FCSTD DOCUMENT  (FreeCAD 0.20R29603 (Git))
Label: Heat Exchanger inlet dispersion grid rounded edges - 100mm
License: All rights reserved
LicenseURL: http://en.wikipedia.org/wiki/All_rights_reserved
objects: Sketcher::SketchObject×6, PartDesign::Body×1
note: 7 computed .brp shape members not serialized (recipe doc carries the construction recipe); baked Part::Feature solids carry a one-line shape summary decoded from their .brp

FEATURE [Sketcher::SketchObject] Sketch
  FullyConstrained = false
  MapMode = 5
  Support = -> [XY_Plane]
  sketch-geometry (86):
    g0: ArcOfCircle CenterX=0 CenterY=0 CenterZ=0 NormalX=0 NormalY=0 NormalZ=1 AngleXU=0 Radius=114.286 StartAngle=0 EndAngle=1.5708
    g1: LineSegment StartX=32.431 StartY=109.588 StartZ=0 EndX=49.5867 EndY=102.968 EndZ=0
    g2: LineSegment StartX=56.0034 StartY=99.6235 StartZ=0 EndX=71.256 EndY=89.3522 EndZ=0
    g3: LineSegment StartX=76.7676 StartY=84.6638 StartZ=0 EndX=89.3522 EndY=71.256 EndZ=0
    g4: LineSegment StartX=93.6823 StartY=65.4587 StartZ=0 EndX=102.968 EndY=49.5867 EndZ=0
    g5: LineSegment StartX=105.903 StartY=42.9634 StartZ=0 EndX=111.422 EndY=25.4227 EndZ=0
    g6: LineSegment StartX=14.2857 StartY=2.955e-12 StartZ=0 EndX=0 EndY=2.955e-12 EndZ=0
    g7: LineSegment StartX=28.5714 StartY=2.955e-12 StartZ=0 EndX=14.2857 EndY=2.955e-12 EndZ=0
    g8: LineSegment StartX=57.1429 StartY=2.955e-12 StartZ=0 EndX=42.8571 EndY=2.955e-12 EndZ=0
    g9: LineSegment StartX=42.8571 StartY=2.955e-12 StartZ=0 EndX=28.5714 EndY=2.955e-12 EndZ=0
    g10: LineSegment StartX=71.4286 StartY=2.955e-12 StartZ=0 EndX=57.1429 EndY=2.955e-12 EndZ=0
    g11: LineSegment StartX=85.7143 StartY=2.955e-12 StartZ=0 EndX=71.4286 EndY=2.955e-12 EndZ=0
    g12: LineSegment StartX=85.7143 StartY=2.955e-12 StartZ=0 EndX=100 EndY=2.955e-12 EndZ=0
    g13: LineSegment StartX=100 StartY=2.955e-12 StartZ=0 EndX=114.286 EndY=2.955e-12 EndZ=0
    g14: LineSegment StartX=14.2857 StartY=2.955e-12 StartZ=0 EndX=14.2857 EndY=10 EndZ=0
    g15: LineSegment StartX=32.431 StartY=109.588 StartZ=0 EndX=28.9234 EndY=9.9938 EndZ=0
    g16: LineSegment StartX=28.9234 StartY=9.9938 StartZ=0 EndX=28.5714 EndY=2.9559e-12 EndZ=0
    g17: LineSegment StartX=56.0034 StartY=99.6235 StartZ=0 EndX=44.1654 EndY=9.91405 EndZ=0
    g18: LineSegment StartX=44.1654 StartY=9.91405 StartZ=0 EndX=42.8571 EndY=2.9559e-12 EndZ=0
    g19: LineSegment StartX=76.7676 StartY=84.6638 StartZ=0 EndX=59.4009 EndY=9.74172 EndZ=0
    g20: LineSegment StartX=59.4009 StartY=9.74172 StartZ=0 EndX=57.1429 EndY=2.9559e-12 EndZ=0
    g21: LineSegment StartX=93.6823 StartY=65.4587 StartZ=0 EndX=74.6473 EndY=9.46782 EndZ=0
    g22: LineSegment StartX=74.6473 StartY=9.46782 StartZ=0 EndX=71.4286 EndY=2.9559e-12 EndZ=0
    g23: LineSegment StartX=105.903 StartY=42.9634 StartZ=0 EndX=89.9671 EndY=9.05059 EndZ=0
    g24: LineSegment StartX=89.9671 StartY=9.05059 StartZ=0 EndX=85.7143 EndY=2.9559e-12 EndZ=0
    g25: GeomPoint X=65.1429 Y=157.269 Z=0
    g26: Circle CenterX=49.5867 CenterY=102.968 CenterZ=0 NormalX=0 NormalY=0 NormalZ=1 AngleXU=0 Radius=1
    g27: Circle CenterX=30.8258 CenterY=64.0104 CenterZ=0 NormalX=0 NormalY=0 NormalZ=1 AngleXU=0 Radius=1
    g28: Circle CenterX=28.9234 CenterY=9.9938 CenterZ=0 NormalX=0 NormalY=0 NormalZ=1 AngleXU=0 Radius=1
    g29: BSplineCurve PolesCount=3 KnotsCount=2 Degree=2 IsPeriodic=0
    g30: GeomPoint X=49.5867 Y=102.968 Z=0
    g31: GeomPoint X=28.9234 Y=9.9938 Z=0
    g32: LineSegment StartX=49.5867 StartY=102.968 StartZ=0 EndX=30.8258 EndY=64.0104 EndZ=0
    g33: Circle CenterX=71.256 CenterY=89.3522 CenterZ=0 NormalX=0 NormalY=0 NormalZ=1 AngleXU=0 Radius=1
    g34: Circle CenterX=51.3549 CenterY=64.3971 CenterZ=0 NormalX=0 NormalY=0 NormalZ=1 AngleXU=0 Radius=1
    g35: Circle CenterX=44.1654 CenterY=9.91405 CenterZ=0 NormalX=0 NormalY=0 NormalZ=1 AngleXU=0 Radius=1
    g36: BSplineCurve PolesCount=3 KnotsCount=2 Degree=2 IsPeriodic=0
    g37: GeomPoint X=71.256 Y=89.3522 Z=0
    g38: GeomPoint X=44.1654 Y=9.91405 Z=0
    g39: LineSegment StartX=71.256 StartY=89.3522 StartZ=0 EndX=51.3549 EndY=64.3971 EndZ=0
    g40: Circle CenterX=59.4009 CenterY=9.74172 CenterZ=0 NormalX=0 NormalY=0 NormalZ=1 AngleXU=0 Radius=1
    g41: Circle CenterX=70.1011 CenterY=55.9038 CenterZ=0 NormalX=0 NormalY=0 NormalZ=1 AngleXU=0 Radius=1
    g42: Circle CenterX=89.3522 CenterY=71.256 CenterZ=0 NormalX=0 NormalY=0 NormalZ=1 AngleXU=0 Radius=1
    g43: BSplineCurve PolesCount=3 KnotsCount=2 Degree=2 IsPeriodic=0
    g44: GeomPoint X=59.4009 Y=9.74172 Z=0
    g45: GeomPoint X=89.3522 Y=71.256 Z=0
    g46: Circle CenterX=74.6473 CenterY=9.46782 CenterZ=0 NormalX=0 NormalY=0 NormalZ=1 AngleXU=0 Radius=1
    g47: Circle CenterX=85.4122 CenterY=41.1323 CenterZ=0 NormalX=0 NormalY=0 NormalZ=1 AngleXU=0 Radius=1
    g48: Circle CenterX=102.968 CenterY=49.5867 CenterZ=0 NormalX=0 NormalY=0 NormalZ=1 AngleXU=0 Radius=1
    g49: BSplineCurve PolesCount=3 KnotsCount=2 Degree=2 IsPeriodic=0
    g50: GeomPoint X=74.6473 Y=9.46782 Z=0
    g51: GeomPoint X=102.968 Y=49.5867 Z=0
    g52: Circle CenterX=89.9671 CenterY=9.05059 CenterZ=0 NormalX=0 NormalY=0 NormalZ=1 AngleXU=0 Radius=1
    g53: Circle CenterX=96.0077 CenterY=21.9056 CenterZ=0 NormalX=0 NormalY=0 NormalZ=1 AngleXU=0 Radius=1
    g54: Circle CenterX=111.422 CenterY=25.4227 CenterZ=0 NormalX=0 NormalY=0 NormalZ=1 AngleXU=0 Radius=1
    g55: BSplineCurve PolesCount=3 KnotsCount=2 Degree=2 IsPeriodic=0
    g56: GeomPoint X=89.9671 Y=9.05059 Z=0
    g57: GeomPoint X=111.422 Y=25.4227 Z=0
    g58: LineSegment StartX=70.1011 StartY=55.9038 StartZ=0 EndX=89.3522 EndY=71.256 EndZ=0
    g59: LineSegment StartX=85.4122 StartY=41.1323 StartZ=0 EndX=102.968 EndY=49.5867 EndZ=0
    g60: LineSegment StartX=96.0077 StartY=21.9056 StartZ=0 EndX=111.422 EndY=25.4227 EndZ=0
    g61: LineSegment StartX=100 StartY=2.955e-12 StartZ=0 EndX=103.536 EndY=3.53553 EndZ=0
    g62: ArcOfCircle CenterX=106.685 CenterY=0.385781 CenterZ=0 NormalX=0 NormalY=0 NormalZ=1 AngleXU=0 Radius=4.45442 StartAngle=0.436669 EndAngle=2.35619
    g63: ArcOfCircle CenterX=114.286 CenterY=3.93303 CenterZ=0 NormalX=0 NormalY=0 NormalZ=1 AngleXU=0 Radius=3.93303 StartAngle=3.57826 EndAngle=4.71239
    g64: LineSegment StartX=114.286 StartY=2.955e-12 StartZ=0 EndX=111.42 EndY=25.431 EndZ=0
    g65: LineSegment StartX=111.42 StartY=25.431 StartZ=0 EndX=102.968 EndY=49.5867 EndZ=0
    g66: LineSegment StartX=102.968 StartY=49.5867 StartZ=0 EndX=89.3522 EndY=71.256 EndZ=0
    g67: LineSegment StartX=89.3522 StartY=71.256 StartZ=0 EndX=71.256 EndY=89.3522 EndZ=0
    g68: LineSegment StartX=71.256 StartY=89.3522 StartZ=0 EndX=49.5867 EndY=102.968 EndZ=0
    g69: LineSegment StartX=49.5867 StartY=102.968 StartZ=0 EndX=25.431 EndY=111.42 EndZ=0
    g70: LineSegment StartX=25.431 StartY=111.42 StartZ=0 EndX=7.1e-15 EndY=114.286 EndZ=0
    g71: LineSegment StartX=7.2323 StartY=114.057 StartZ=0 EndX=25.431 EndY=111.42 EndZ=0
    g72: LineSegment StartX=14.2857 StartY=10 StartZ=0 EndX=14.2857 EndY=113.389 EndZ=0
    g73: Circle CenterX=14.2857 CenterY=10 CenterZ=0 NormalX=0 NormalY=0 NormalZ=1 AngleXU=0 Radius=1
    g74: Circle CenterX=14.2857 CenterY=62.5898 CenterZ=0 NormalX=0 NormalY=0 NormalZ=1 AngleXU=0 Radius=1
    g75: Circle CenterX=25.431 CenterY=111.42 CenterZ=0 NormalX=0 NormalY=0 NormalZ=1 AngleXU=0 Radius=1
    g76: BSplineCurve PolesCount=3 KnotsCount=2 Degree=2 IsPeriodic=0
    g77: GeomPoint X=14.2857 Y=10 Z=0
    g78: GeomPoint X=25.431 Y=111.42 Z=0
    g79: LineSegment StartX=25.431 StartY=111.42 StartZ=0 EndX=14.2857 EndY=62.5898 EndZ=0
    g80: LineSegment StartX=111.422 StartY=25.4227 StartZ=0 EndX=114.286 EndY=26.076 EndZ=0
    g81: LineSegment StartX=102.968 StartY=49.5867 StartZ=0 EndX=105.614 EndY=50.8611 EndZ=0
    g82: LineSegment StartX=89.3522 StartY=71.256 StartZ=0 EndX=91.6485 EndY=73.0872 EndZ=0
    g83: LineSegment StartX=71.256 StartY=89.3522 StartZ=0 EndX=73.0872 EndY=91.6485 EndZ=0
    g84: LineSegment StartX=49.5867 StartY=102.968 StartZ=0 EndX=50.8611 EndY=105.614 EndZ=0
    g85: LineSegment StartX=25.431 StartY=111.42 StartZ=0 EndX=26.0845 EndY=114.284 EndZ=0
  constraints (208):
    c: Coincident(g0,g-1)
    c: PointOnObject(g0,g-2)
    c: PointOnObject(g1,g0)
    c: PointOnObject(g1,g0)
    c: PointOnObject(g2,g0)
    c: PointOnObject(g2,g0)
    c: PointOnObject(g3,g0)
    c: PointOnObject(g3,g0)
    c: PointOnObject(g4,g0)
    c: PointOnObject(g4,g0)
    c: PointOnObject(g5,g0)
    c: PointOnObject(g5,g0)
    c: PointOnObject(g6,g-2)
    c: Coincident(g7,g6)
    c: Horizontal(g6)
    c: Coincident(g10,g8)
    c: Coincident(g9,g7)
    c: Horizontal(g7)
    c: Coincident(g8,g9)
    c: Horizontal(g8)
    c: Horizontal(g9)
    c: Coincident(g11,g10)
    c: Horizontal(g10)
    c: Horizontal(g11)
    c: Equal(g6,g7)
    c: Equal(g7,g9)
    c: Equal(g9,g8)
    c: Equal(g8,g10)
    c: Equal(g10,g11)
    c: Coincident(g16,g7)
    c: Coincident(g18,g8)
    c: Coincident(g20,g8)
    c: Coincident(g22,g10)
    c: PointOnObject(g0,g-1)
    c: Coincident(g12,g11)
    c: Horizontal(g12)
    c: Coincident(g13,g12)
    c: Coincident(g13,g0)
    c: Horizontal(g13)
    c: Equal(g11,g12)
    c: Equal(g12,g13)
    c: Coincident(g24,g11)
    c: Coincident(g14,g6)
    c: Vertical(g14)
    c: Coincident(g15,g16)
    c: Parallel(g16,g15)
    c: Coincident(g17,g18)
    c: Coincident(g19,g20)
    c: Coincident(g21,g22)
    c: Coincident(g23,g24)
    c: Parallel(g23,g24)
    c: Parallel(g21,g22)
    c: Parallel(g19,g20)
    c: Parallel(g17,g18)
    c: Equal(g14,g16)
    c: Equal(g16,g18)
    c: Equal(g18,g20)
    c: Equal(g20,g22)
    c: Equal(g22,g24)
    c: DistanceY(g14,g14) = 10
    c: Weight(g26) = 1
    c: Equal(g26,g27)
    c: Equal(g26,g28)
    c: InternalAlignment(g26,g29)
    c: InternalAlignment(g27,g29)
    c: InternalAlignment(g28,g29)
    c: InternalAlignment(g30,g29)
    c: InternalAlignment(g31,g29)
    c: Coincident(g26,g1)
    c: Coincident(g32,g1)
    c: Coincident(g32,g27)
    c: Coincident(g28,g15)
    c: PointOnObject(g27,g15)
    c: Perpendicular(g0,g32)
    c: Weight(g33) = 1
    c: Coincident(g36,g2)
    c: Equal(g33,g34)
    c: PointOnObject(g34,g17)
    c: Equal(g33,g35)
    c: Coincident(g36,g17)
    c: InternalAlignment(g33,g36)
    c: InternalAlignment(g34,g36)
    c: InternalAlignment(g35,g36)
    c: InternalAlignment(g37,g36)
    c: InternalAlignment(g38,g36)
    c: Coincident(g39,g2)
    c: Coincident(g39,g34)
    c: Perpendicular(g0,g39)
    c: Weight(g40) = 1
    c: Coincident(g43,g19)
    c: Equal(g40,g41)
    c: PointOnObject(g41,g19)
    c: Equal(g40,g42)
    c: Coincident(g43,g3)
    c: InternalAlignment(g40,g43)
    c: InternalAlignment(g41,g43)
    c: InternalAlignment(g42,g43)
    c: InternalAlignment(g44,g43)
    c: InternalAlignment(g45,g43)
    c: Weight(g46) = 1
    c: Coincident(g49,g21)
    c: Equal(g46,g47)
    c: PointOnObject(g47,g21)
    c: Equal(g46,g48)
    c: Coincident(g49,g4)
    c: InternalAlignment(g46,g49)
    c: InternalAlignment(g47,g49)
    c: InternalAlignment(g48,g49)
    c: InternalAlignment(g50,g49)
    c: InternalAlignment(g51,g49)
    c: Weight(g52) = 1
    c: Coincident(g55,g23)
    c: Equal(g52,g53)
    c: PointOnObject(g53,g23)
    c: Equal(g52,g54)
    c: Coincident(g55,g5)
    c: InternalAlignment(g52,g55)
    c: InternalAlignment(g53,g55)
    c: InternalAlignment(g54,g55)
    c: InternalAlignment(g56,g55)
    c: InternalAlignment(g57,g55)
    c: Coincident(g58,g41)
    c: Coincident(g58,g3)
    c: Coincident(g59,g47)
    c: Coincident(g59,g4)
    c: Coincident(g60,g53)
    c: Coincident(g60,g5)
    c: Perpendicular(g0,g58)
    c: Perpendicular(g0,g59)
    c: Perpendicular(g0,g60)
    c: Coincident(g61,g12)
    c: Distance(g61) = 5
    c: Coincident(g0,g63)
    c: Coincident(g63,g64)
    c: Coincident(g64,g65)
    c: Coincident(g65,g49)
    c: Coincident(g65,g66)
    c: Coincident(g66,g43)
    c: Coincident(g66,g67)
    c: Coincident(g67,g36)
    c: Coincident(g67,g68)
    c: Coincident(g68,g29)
    c: Coincident(g68,g69)
    c: Coincident(g69,g70)
    c: Coincident(g70,g0)
    c: Equal(g70,g69)
    c: Equal(g69,g68)
    c: Equal(g68,g67)
    c: Equal(g67,g66)
    c: Equal(g66,g65)
    c: Equal(g65,g64)
    c: Coincident(g23,g5)
    c: Coincident(g4,g21)
    c: Coincident(g19,g3)
    c: Coincident(g2,g17)
    c: Coincident(g15,g1)
    c: Coincident(g71,g69)
    c: PointOnObject(g69,g0)
    c: Equal(g71,g1)
    c: Equal(g1,g2)
    c: Equal(g2,g3)
    c: Equal(g3,g4)
    c: Equal(g4,g5)
    c: PointOnObject(g64,g0)
    c: PointOnObject(g71,g0)
    c: DistanceX(g69,g1) = 7
    c: Coincident(g72,g14)
    c: PointOnObject(g72,g0)
    c: Vertical(g72)
    c: Weight(g73) = 1
    c: Coincident(g76,g14)
    c: Equal(g73,g74)
    c: PointOnObject(g74,g72)
    c: Equal(g73,g75)
    c: Coincident(g76,g69)
    c: InternalAlignment(g73,g76)
    c: InternalAlignment(g74,g76)
    c: InternalAlignment(g75,g76)
    c: InternalAlignment(g77,g76)
    c: InternalAlignment(g78,g76)
    c: Coincident(g79,g76)
    c: Coincident(g79,g74)
    c: Perpendicular(g0,g79)
    c: Angle(g13,g61) = 0.785398
    c: DistanceX(g14,g63) = 100
    c: Block(g60)
    c: Tangent(g63,g13)
    c: Tangent(g63,g62) = 1.5708
    c: Tangent(g62,g61) = 1.5708
    c: Block(g62)
    c: Coincident(g80,g55)
    c: Perpendicular(g0,g80)
    c: DistanceX(g63,g80) = 0
    c: Coincident(g81,g49)
    c: Coincident(g82,g43)
    c: Coincident(g83,g36)
    c: Coincident(g84,g29)
    c: Coincident(g85,g76)
    c: Perpendicular(g0,g85)
    c: Perpendicular(g0,g84)
    c: Perpendicular(g0,g83)
    c: Perpendicular(g0,g82)
    c: Perpendicular(g0,g81)
    c: Equal(g85,g84)
    c: Equal(g84,g83)
    c: Equal(g83,g82)
    c: Equal(g82,g81)
    c: Equal(g81,g80)
FEATURE [Sketcher::SketchObject] Sketch001
  ExternalGeometry = -> [Sketch]
  FullyConstrained = false
  MapMode = 5
  Support = -> [XY_Plane]
  sketch-geometry (118):
    g0: LineSegment StartX=100 StartY=2.955e-12 StartZ=0 EndX=100 EndY=-15 EndZ=0
    g1: LineSegment StartX=14.2857 StartY=2.9541e-12 StartZ=0 EndX=14.2857 EndY=-15 EndZ=0
    g2: LineSegment StartX=14.2857 StartY=10 StartZ=0 EndX=14.2857 EndY=115.18 EndZ=0
    g3: LineSegment StartX=28.9234 StartY=9.9938 StartZ=0 EndX=32.403 EndY=108.793 EndZ=0
    g4: LineSegment StartX=44.1654 StartY=9.91405 StartZ=0 EndX=55.6558 EndY=96.9892 EndZ=0
    g5: LineSegment StartX=59.4009 StartY=9.74172 StartZ=0 EndX=75.7744 EndY=80.3789 EndZ=0
    g6: LineSegment StartX=74.6473 StartY=9.46782 StartZ=0 EndX=91.8032 EndY=59.9313 EndZ=0
    g7: LineSegment StartX=89.9671 StartY=9.05059 StartZ=0 EndX=103.13 EndY=37.0622 EndZ=0
    g8: LineSegment StartX=103.536 StartY=3.53553 StartZ=0 EndX=112.735 EndY=12.735 EndZ=0
    g9: LineSegment StartX=10.2857 StartY=10 StartZ=0 EndX=10.2857 EndY=115.18 EndZ=0
    g10: LineSegment StartX=24.9259 StartY=10.1346 StartZ=0 EndX=28.4054 EndY=108.933 EndZ=0
    g11: LineSegment StartX=40.1998 StartY=10.4374 StartZ=0 EndX=51.6902 EndY=97.5125 EndZ=0
    g12: LineSegment StartX=55.5043 StartY=10.645 StartZ=0 EndX=71.8777 EndY=81.2821 EndZ=0
    g13: LineSegment StartX=70.8602 StartY=10.7553 StartZ=0 EndX=88.0161 EndY=61.2188 EndZ=0
    g14: LineSegment StartX=86.3469 StartY=10.7517 StartZ=0 EndX=99.5095 EndY=38.7633 EndZ=0
    g15: LineSegment StartX=102.828 StartY=-2.82843 StartZ=0 EndX=115.563 EndY=9.90657 EndZ=0
    g16: LineSegment StartX=99.5095 StartY=38.7633 StartZ=0 EndX=103.13 EndY=37.0622 EndZ=0
    g17: LineSegment StartX=88.0161 StartY=61.2188 StartZ=0 EndX=91.8032 EndY=59.9313 EndZ=0
    g18: LineSegment StartX=71.8777 StartY=81.2821 StartZ=0 EndX=75.7744 EndY=80.3789 EndZ=0
    g19: LineSegment StartX=51.6902 StartY=97.5125 StartZ=0 EndX=55.6558 EndY=96.9892 EndZ=0
    g20: LineSegment StartX=28.4054 StartY=108.933 StartZ=0 EndX=32.403 EndY=108.793 EndZ=0
    g21: LineSegment StartX=10.2857 StartY=115.18 StartZ=0 EndX=14.2857 EndY=115.18 EndZ=0
    g22: LineSegment StartX=85.4937 StartY=-0.469334 StartZ=0 EndX=74.474 EndY=8.95808 EndZ=0
    g23: LineSegment StartX=71.2571 StartY=-0.504511 StartZ=0 EndX=59.2754 EndY=9.19999 EndZ=0
    g24: LineSegment StartX=57.019 StartY=-0.53455 StartZ=0 EndX=44.09 EndY=9.34247 EndZ=0
    g25: LineSegment StartX=42.783 StartY=-0.562109 StartZ=0 EndX=28.9023 EndY=9.39365 EndZ=0
    g26: LineSegment StartX=28.5505 StartY=-0.595643 StartZ=0 EndX=14.2857 EndY=9.38967 EndZ=0
    g27: LineSegment StartX=74.6473 StartY=9.46782 StartZ=0 EndX=82.5619 EndY=2.69685 EndZ=0
    g28: LineSegment StartX=82.5619 StartY=2.69685 StartZ=0 EndX=85.7143 EndY=2.9559e-12 EndZ=0
    g29: LineSegment StartX=59.4009 StartY=9.74172 StartZ=0 EndX=68.1159 EndY=2.68309 EndZ=0
    g30: LineSegment StartX=68.1159 StartY=2.68309 StartZ=0 EndX=71.4286 EndY=2.9559e-12 EndZ=0
    g31: LineSegment StartX=44.1654 StartY=9.91405 StartZ=0 EndX=53.6545 EndY=2.6649 EndZ=0
    g32: LineSegment StartX=53.6545 StartY=2.6649 StartZ=0 EndX=57.1429 EndY=2.9559e-12 EndZ=0
    g33: LineSegment StartX=28.9234 StartY=9.9938 StartZ=0 EndX=39.1713 EndY=2.64361 EndZ=0
    g34: LineSegment StartX=39.1713 StartY=2.64361 StartZ=0 EndX=42.8571 EndY=2.9559e-12 EndZ=0
    g35: LineSegment StartX=14.2857 StartY=10 StartZ=0 EndX=24.6652 EndY=2.73433 EndZ=0
    g36: LineSegment StartX=24.6652 StartY=2.73433 StartZ=0 EndX=28.5714 EndY=2.9559e-12 EndZ=0
    g37: LineSegment StartX=40.1998 StartY=10.4374 StartZ=0 EndX=39.1713 EndY=2.64361 EndZ=0
    g38: LineSegment StartX=24.9259 StartY=10.1346 StartZ=0 EndX=24.6652 EndY=2.73433 EndZ=0
    g39: LineSegment StartX=55.5043 StartY=10.645 StartZ=0 EndX=53.6545 EndY=2.6649 EndZ=0
    g40: LineSegment StartX=70.8602 StartY=10.7553 StartZ=0 EndX=68.1159 EndY=2.68309 EndZ=0
    g41: LineSegment StartX=86.3469 StartY=10.7517 StartZ=0 EndX=82.5619 EndY=2.69685 EndZ=0
    g42: LineSegment StartX=112.735 StartY=12.735 StartZ=0 EndX=115.563 EndY=9.90657 EndZ=0
    g43: LineSegment StartX=89.9671 StartY=9.05059 StartZ=0 EndX=103.536 EndY=3.53553 EndZ=0
    g44: LineSegment StartX=89.7542 StartY=8.59742 StartZ=0 EndX=103.152 EndY=3.15179 EndZ=0
    g45: LineSegment StartX=100 StartY=2.955e-12 StartZ=0 EndX=102.828 EndY=-2.82843 EndZ=0
    g46: LineSegment StartX=93.6424 StartY=7.01699 StartZ=0 EndX=93.8307 EndY=7.48019 EndZ=0
    g47: LineSegment StartX=79.2582 StartY=4.86517 StartZ=0 EndX=79.5833 EndY=5.24511 EndZ=0
    g48: LineSegment StartX=64.4662 StartY=4.99567 StartZ=0 EndX=64.7809 EndY=5.38422 EndZ=0
    g49: LineSegment StartX=49.4204 StartY=5.27034 StartZ=0 EndX=49.7239 EndY=5.66766 EndZ=0
    g50: LineSegment StartX=34.899 StartY=5.09256 StartZ=0 EndX=35.1904 EndY=5.49886 EndZ=0
    g51: LineSegment StartX=20.4371 StartY=5.08367 StartZ=0 EndX=20.7239 EndY=5.49328 EndZ=0
    g52: LineSegment StartX=24.6652 StartY=2.73433 StartZ=0 EndX=28.6628 EndY=2.59354 EndZ=0
    g53: LineSegment StartX=28.9234 StartY=9.9938 StartZ=0 EndX=28.5714 EndY=2.9559e-12 EndZ=0
    g54: LineSegment StartX=44.1654 StartY=9.91405 StartZ=0 EndX=42.8571 EndY=2.9559e-12 EndZ=0
    g55: LineSegment StartX=39.1713 StartY=2.64361 StartZ=0 EndX=43.1369 EndY=2.12031 EndZ=0
    g56: LineSegment StartX=59.4009 StartY=9.74172 StartZ=0 EndX=57.1429 EndY=2.9559e-12 EndZ=0
    g57: LineSegment StartX=53.6545 StartY=2.6649 StartZ=0 EndX=57.5512 EndY=1.76166 EndZ=0
    g58: LineSegment StartX=74.6473 StartY=9.46782 StartZ=0 EndX=71.4286 EndY=2.9559e-12 EndZ=0
    g59: LineSegment StartX=68.1159 StartY=2.68309 StartZ=0 EndX=71.903 EndY=1.39559 EndZ=0
    g60: LineSegment StartX=89.9671 StartY=9.05059 StartZ=0 EndX=85.7143 EndY=2.9559e-12 EndZ=0
    g61: LineSegment StartX=82.5619 StartY=2.69685 StartZ=0 EndX=86.1822 EndY=0.99571 EndZ=0
    g62: LineSegment StartX=103.536 StartY=3.53553 StartZ=0 EndX=100 EndY=2.955e-12 EndZ=0
    g63: LineSegment StartX=10.2857 StartY=115.18 StartZ=0 EndX=4.78571 EndY=115.18 EndZ=0
    g64: LineSegment StartX=4.78571 StartY=115.18 StartZ=0 EndX=4.78571 EndY=115.68 EndZ=0
    g65: LineSegment StartX=4.78571 StartY=115.68 StartZ=0 EndX=19.7857 EndY=115.68 EndZ=0
    g66: LineSegment StartX=19.7857 StartY=115.68 StartZ=0 EndX=19.7857 EndY=115.18 EndZ=0
    g67: LineSegment StartX=19.7857 StartY=115.18 StartZ=0 EndX=14.2857 EndY=115.18 EndZ=0
    g68: LineSegment StartX=28.4054 StartY=108.933 StartZ=0 EndX=22.9088 EndY=109.127 EndZ=0
    g69: LineSegment StartX=22.9088 StartY=109.127 StartZ=0 EndX=22.9264 EndY=109.627 EndZ=0
    g70: LineSegment StartX=22.9264 StartY=109.627 StartZ=0 EndX=37.9172 EndY=109.099 EndZ=0
    g71: LineSegment StartX=37.9172 StartY=109.099 StartZ=0 EndX=37.8996 EndY=108.599 EndZ=0
    g72: LineSegment StartX=37.8996 StartY=108.599 StartZ=0 EndX=32.403 EndY=108.793 EndZ=0
    g73: LineSegment StartX=51.6902 StartY=97.5125 StartZ=0 EndX=46.2374 EndY=98.232 EndZ=0
    g74: LineSegment StartX=46.2374 StartY=98.232 StartZ=0 EndX=46.3028 EndY=98.7277 EndZ=0
    g75: LineSegment StartX=46.3028 StartY=98.7277 StartZ=0 EndX=61.1739 EndY=96.7654 EndZ=0
    g76: LineSegment StartX=61.1739 StartY=96.7654 StartZ=0 EndX=61.1085 EndY=96.2697 EndZ=0
    g77: LineSegment StartX=61.1085 StartY=96.2697 StartZ=0 EndX=55.6558 EndY=96.9892 EndZ=0
    g78: LineSegment StartX=71.8777 StartY=81.2821 StartZ=0 EndX=66.5197 EndY=82.5241 EndZ=0
    g79: LineSegment StartX=66.5197 StartY=82.5241 StartZ=0 EndX=66.6326 EndY=83.0112 EndZ=0
    g80: LineSegment StartX=66.6326 StartY=83.0112 StartZ=0 EndX=81.2452 EndY=79.624 EndZ=0
    g81: LineSegment StartX=81.2452 StartY=79.624 StartZ=0 EndX=81.1323 EndY=79.1369 EndZ=0
    g82: LineSegment StartX=81.1323 StartY=79.1369 StartZ=0 EndX=75.7744 EndY=80.3789 EndZ=0
    g83: LineSegment StartX=88.0161 StartY=61.2188 StartZ=0 EndX=82.8088 EndY=62.9891 EndZ=0
    g84: LineSegment StartX=82.8088 StartY=62.9891 StartZ=0 EndX=82.9697 EndY=63.4625 EndZ=0
    g85: LineSegment StartX=82.9697 StartY=63.4625 StartZ=0 EndX=97.1715 EndY=58.6344 EndZ=0
    g86: LineSegment StartX=97.1715 StartY=58.6344 StartZ=0 EndX=97.0105 EndY=58.161 EndZ=0
    g87: LineSegment StartX=97.0105 StartY=58.161 StartZ=0 EndX=91.8032 EndY=59.9313 EndZ=0
    g88: LineSegment StartX=99.5095 StartY=38.7633 StartZ=0 EndX=94.5316 EndY=41.1024 EndZ=0
    g89: LineSegment StartX=94.5316 StartY=41.1024 StartZ=0 EndX=94.7443 EndY=41.5549 EndZ=0
    g90: LineSegment StartX=94.7443 StartY=41.5549 StartZ=0 EndX=108.32 EndY=35.1756 EndZ=0
    g91: LineSegment StartX=108.32 StartY=35.1756 StartZ=0 EndX=108.108 EndY=34.7231 EndZ=0
    g92: LineSegment StartX=108.108 StartY=34.7231 StartZ=0 EndX=103.13 EndY=37.0622 EndZ=0
    g93: LineSegment StartX=112.735 StartY=12.735 StartZ=0 EndX=108.846 EndY=16.6241 EndZ=0
    g94: LineSegment StartX=108.846 StartY=16.6241 StartZ=0 EndX=109.199 EndY=16.9776 EndZ=0
    g95: LineSegment StartX=109.199 StartY=16.9776 StartZ=0 EndX=119.806 EndY=6.37103 EndZ=0
    g96: LineSegment StartX=119.806 StartY=6.37103 StartZ=0 EndX=119.453 EndY=6.01748 EndZ=0
    g97: LineSegment StartX=119.453 StartY=6.01748 StartZ=0 EndX=115.563 EndY=9.90657 EndZ=0
    g98: LineSegment StartX=102.828 StartY=-2.82843 StartZ=0 EndX=106.718 EndY=-6.71751 EndZ=0
    g99: LineSegment StartX=106.718 StartY=-6.71751 StartZ=0 EndX=106.364 EndY=-7.07107 EndZ=0
    g100: LineSegment StartX=106.364 StartY=-7.07107 StartZ=0 EndX=100.5 EndY=-1.20711 EndZ=0
    g101: LineSegment StartX=100.5 StartY=-1.20711 StartZ=0 EndX=100.5 EndY=-15 EndZ=0
    g102: LineSegment StartX=10.2857 StartY=0 StartZ=0 EndX=10.2857 EndY=10 EndZ=0
    g103: LineSegment StartX=13.7857 StartY=-15 StartZ=0 EndX=13.7857 EndY=-0.5 EndZ=0
    g104: LineSegment StartX=13.7857 StartY=-0.5 StartZ=0 EndX=5.49282 EndY=-0.5 EndZ=0
    g105: LineSegment StartX=5.49282 StartY=-0.5 StartZ=0 EndX=5.49282 EndY=0 EndZ=0
    g106: LineSegment StartX=5.49282 StartY=0 StartZ=0 EndX=10.2857 EndY=0 EndZ=0
    g107: LineSegment StartX=13.7857 StartY=-0.5 StartZ=0 EndX=14.2857 EndY=-0.5 EndZ=0
    g108: LineSegment StartX=42.8571 StartY=2.9559e-12 StartZ=0 EndX=42.783 EndY=-0.562109 EndZ=0
    g109: LineSegment StartX=28.5714 StartY=2.9559e-12 StartZ=0 EndX=28.5505 EndY=-0.595643 EndZ=0
    g110: LineSegment StartX=57.1429 StartY=2.9559e-12 StartZ=0 EndX=57.019 EndY=-0.53455 EndZ=0
    g111: LineSegment StartX=71.2571 StartY=-0.504511 StartZ=0 EndX=71.4286 EndY=2.9559e-12 EndZ=0
    g112: LineSegment StartX=85.7143 StartY=2.9559e-12 StartZ=0 EndX=85.4937 EndY=-0.469334 EndZ=0
    g113: LineSegment StartX=10.2857 StartY=0 StartZ=0 EndX=14.2857 EndY=2.9541e-12 EndZ=0
    g114: LineSegment StartX=14.2857 StartY=9.38967 StartZ=0 EndX=14.2857 EndY=2.9541e-12 EndZ=0
    g115: LineSegment StartX=14.2857 StartY=10 StartZ=0 EndX=14.2857 EndY=9.38967 EndZ=0
    g116: LineSegment StartX=100.5 StartY=-15 StartZ=0 EndX=100 EndY=-15 EndZ=0
    g117: LineSegment StartX=13.7857 StartY=-15 StartZ=0 EndX=14.2857 EndY=-15 EndZ=0
  constraints (318):
    c: Vertical(g0)
    c: Vertical(g1)
    c: DistanceY(g1,g1) = 15
    c: Coincident(g-3,g1)
    c: Coincident(g0,g-9)
    c: Distance(g2) = 105.18
    c: Distance(g3) = 98.86
    c: Distance(g4) = 87.83
    c: Distance(g5) = 72.51
    c: Distance(g6) = 53.3
    c: Distance(g7) = 30.95
    c: Distance(g8) = 13.01
    c: Tangent(g2,g-3) = -1.5708
    c: Tangent(g3,g-4) = 1.5708
    c: Tangent(g4,g-5) = 1.5708
    c: Tangent(g5,g-6) = 1.5708
    c: Tangent(g6,g-7) = 1.5708
    c: Tangent(g7,g-8) = 1.5708
    c: Equal(g2,g9) = 105.18
    c: Equal(g3,g10) = 98.86
    c: Equal(g4,g11) = 87.83
    c: Equal(g5,g12) = 72.51
    c: Equal(g6,g13) = 53.3
    c: Equal(g7,g14) = 30.95
    c: Tangent(g8,g-9) = -1.5708
    c: Coincident(g16,g14)
    c: Coincident(g16,g7)
    c: Coincident(g17,g13)
    c: Coincident(g17,g6)
    c: Coincident(g18,g12)
    c: Coincident(g18,g5)
    c: Coincident(g19,g11)
    c: Coincident(g19,g4)
    c: Coincident(g20,g10)
    c: Coincident(g20,g3)
    c: Coincident(g21,g9)
    c: Coincident(g21,g2)
    c: Parallel(g9,g2)
    c: Parallel(g10,g3)
    c: Parallel(g11,g4)
    c: Parallel(g12,g5)
    c: Parallel(g13,g6)
    c: Parallel(g14,g7)
    c: Parallel(g15,g8)
    c: Perpendicular(g21,g9)
    c: Perpendicular(g20,g10)
    c: Perpendicular(g19,g11)
    c: Perpendicular(g18,g12)
    c: Perpendicular(g17,g13)
    c: Perpendicular(g16,g14)
    c: Equal(g16,g17)
    c: Equal(g17,g18)
    c: Equal(g18,g19)
    c: Equal(g19,g20)
    c: Equal(g20,g21)
    c: Distance(g21) = 4
    c: Coincident(g33,g3)
    c: Coincident(g34,g-5)
    c: Coincident(g31,g4)
    c: Coincident(g32,g-6)
    c: Coincident(g29,g5)
    c: Coincident(g30,g-7)
    c: Coincident(g27,g6)
    c: Coincident(g28,g-8)
    c: Coincident(g35,g2)
    c: Coincident(g36,g-4)
    c: PointOnObject(g22,g-7)
    c: PointOnObject(g23,g-6)
    c: PointOnObject(g24,g-5)
    c: PointOnObject(g25,g-4)
    c: PointOnObject(g26,g-3)
    c: Coincident(g27,g28)
    c: Coincident(g29,g30)
    c: Coincident(g31,g32)
    c: Coincident(g33,g34)
    c: Coincident(g35,g36)
    c: Parallel(g29,g30)
    c: Parallel(g27,g28)
    c: Parallel(g31,g32)
    c: Parallel(g33,g34)
    c: Parallel(g35,g36)
    c: Coincident(g37,g11)
    c: Coincident(g37,g33)
    c: Coincident(g38,g10)
    c: Coincident(g38,g35)
    c: Coincident(g39,g12)
    c: Coincident(g39,g31)
    c: Coincident(g40,g13)
    c: Coincident(g40,g29)
    c: Coincident(g41,g14)
    c: Coincident(g41,g27)
    c: Parallel(g26,g35)
    c: Parallel(g25,g33)
    c: Parallel(g24,g31)
    c: Parallel(g23,g29)
    c: Parallel(g22,g27)
    c: Coincident(g42,g8)
    c: Coincident(g42,g15)
    c: Perpendicular(g42,g8)
    c: Equal(g16,g42)
    c: Coincident(g43,g7)
    c: Coincident(g43,g8)
    c: PointOnObject(g44,g-8)
    c: PointOnObject(g44,g-9)
    c: Parallel(g43,g44)
    c: Coincident(g45,g0)
    c: Coincident(g45,g15)
    c: Perpendicular(g15,g45)
    c: PointOnObject(g46,g44)
    c: PointOnObject(g46,g43)
    c: PointOnObject(g47,g22)
    c: PointOnObject(g47,g27)
    c: PointOnObject(g48,g23)
    c: PointOnObject(g48,g29)
    c: PointOnObject(g49,g24)
    c: PointOnObject(g49,g31)
    c: PointOnObject(g50,g25)
    c: PointOnObject(g50,g33)
    c: PointOnObject(g51,g26)
    c: PointOnObject(g51,g35)
    c: Perpendicular(g35,g51)
    c: Perpendicular(g33,g50)
    c: Perpendicular(g31,g49)
    c: Perpendicular(g29,g48)
    c: Perpendicular(g27,g47)
    c: Perpendicular(g46,g44)
    c: Equal(g46,g47)
    c: Equal(g47,g48)
    c: Equal(g48,g49)
    c: Equal(g49,g50)
    c: Equal(g50,g51)
    c: Distance(g51) = 0.5
    c: Parallel(g38,g10)
    c: Parallel(g37,g11)
    c: Parallel(g39,g12)
    c: Parallel(g40,g13)
    c: Parallel(g14,g41)
    c: Coincident(g52,g35)
    c: PointOnObject(g52,g-4)
    c: Coincident(g53,g3)
    c: Coincident(g54,g4)
    c: Coincident(g55,g33)
    c: PointOnObject(g55,g54)
    c: Coincident(g56,g5)
    c: Coincident(g57,g31)
    c: PointOnObject(g57,g56)
    c: Coincident(g58,g6)
    c: Coincident(g59,g29)
    c: PointOnObject(g59,g58)
    c: Coincident(g60,g7)
    c: Coincident(g61,g27)
    c: PointOnObject(g61,g60)
    c: Coincident(g62,g8)
    c: Coincident(g62,g0)
    c: Perpendicular(g52,g53)
    c: Perpendicular(g54,g55)
    c: Perpendicular(g56,g57)
    c: Perpendicular(g58,g59)
    c: Perpendicular(g60,g61)
    c: Coincident(g63,g9)
    c: Horizontal(g63)
    c: Coincident(g63,g64)
    c: Coincident(g64,g65)
    c: Horizontal(g65)
    c: Coincident(g65,g66)
    c: Coincident(g66,g67)
    c: Coincident(g67,g2)
    c: Horizontal(g67)
    c: Coincident(g10,g68)
    c: Coincident(g68,g69)
    c: Coincident(g69,g70)
    c: Coincident(g70,g71)
    c: Coincident(g71,g72)
    c: Coincident(g72,g3)
    c: Coincident(g11,g73)
    c: Coincident(g73,g74)
    c: Coincident(g74,g75)
    c: Coincident(g75,g76)
    c: Coincident(g76,g77)
    c: Coincident(g77,g4)
    c: Coincident(g12,g78)
    c: Coincident(g78,g79)
    c: Coincident(g79,g80)
    c: Coincident(g80,g81)
    c: Coincident(g81,g82)
    c: Coincident(g82,g5)
    c: Coincident(g13,g83)
    c: Coincident(g83,g84)
    c: Coincident(g84,g85)
    c: Coincident(g85,g86)
    c: Coincident(g86,g87)
    c: Coincident(g87,g6)
    c: Coincident(g14,g88)
    c: Coincident(g88,g89)
    c: Coincident(g89,g90)
    c: Coincident(g90,g91)
    c: Coincident(g91,g92)
    c: Coincident(g92,g7)
    c: Coincident(g8,g93)
    c: Coincident(g93,g94)
    c: Coincident(g94,g95)
    c: Coincident(g95,g96)
    c: Coincident(g96,g97)
    c: Coincident(g97,g15)
    c: Coincident(g15,g98)
    c: Coincident(g98,g99)
    c: Coincident(g99,g100)
    c: Coincident(g100,g101)
    c: Vertical(g101)
    c: PointOnObject(g102,g-1)
    c: Coincident(g102,g9)
    c: Vertical(g102)
    c: Vertical(g103)
    c: Coincident(g103,g104)
    c: Horizontal(g104)
    c: Coincident(g104,g105)
    c: PointOnObject(g105,g-1)
    c: Coincident(g105,g106)
    c: Coincident(g106,g102)
    c: Perpendicular(g64,g63)
    c: Perpendicular(g65,g66)
    c: Perpendicular(g70,g69)
    c: Perpendicular(g71,g72)
    c: Perpendicular(g71,g70)
    c: Parallel(g68,g20)
    c: Parallel(g72,g20)
    c: Perpendicular(g73,g74)
    c: Perpendicular(g76,g77)
    c: Parallel(g73,g19)
    c: Parallel(g19,g77)
    c: Parallel(g77,g75)
    c: Perpendicular(g78,g79)
    c: Perpendicular(g81,g82)
    c: Parallel(g78,g18)
    c: Parallel(g18,g82)
    c: Parallel(g82,g80)
    c: Perpendicular(g84,g83)
    c: Perpendicular(g86,g87)
    c: Parallel(g83,g17)
    c: Parallel(g17,g87)
    c: Parallel(g87,g85)
    c: Perpendicular(g89,g88)
    c: Perpendicular(g91,g92)
    c: Parallel(g88,g16)
    c: Parallel(g16,g92)
    c: Parallel(g92,g90)
    c: Perpendicular(g94,g93)
    c: Perpendicular(g96,g97)
    c: Parallel(g93,g42)
    c: Parallel(g42,g95)
    c: Parallel(g95,g97)
    c: Equal(g51,g64)
    c: Equal(g66,g69)
    c: Equal(g69,g74)
    c: Equal(g74,g79)
    c: Equal(g79,g84)
    c: Equal(g84,g89)
    c: Equal(g89,g94)
    c: Equal(g95,g90)
    c: Equal(g90,g85)
    c: Equal(g85,g80)
    c: Equal(g80,g75)
    c: Equal(g75,g70)
    c: Equal(g70,g65)
    c: Distance(g65) = 15
    c: Equal(g67,g72)
    c: Equal(g72,g77)
    c: Equal(g77,g82)
    c: Equal(g82,g87)
    c: Equal(g87,g92)
    c: Equal(g92,g97)
    c: Equal(g63,g67)
    c: Parallel(g45,g98)
    c: Parallel(g100,g98)
    c: Perpendicular(g99,g100)
    c: Equal(g98,g97)
    c: Equal(g99,g96)
    c: Coincident(g107,g103)
    c: PointOnObject(g107,g1)
    c: Horizontal(g107)
    c: Equal(g51,g107)
    c: Equal(g107,g105)
    c: Perpendicular(g105,g104)
    c: Equal(g104,g100)
    c: Coincident(g108,g54)
    c: Coincident(g108,g25)
    c: Parallel(g108,g54)
    c: Coincident(g54,g34)
    c: Coincident(g109,g53)
    c: Coincident(g109,g26)
    c: Parallel(g109,g53)
    c: Coincident(g53,g36)
    c: Coincident(g110,g56)
    c: Coincident(g110,g24)
    c: Parallel(g110,g56)
    c: Coincident(g32,g56)
    c: Coincident(g111,g23)
    c: Coincident(g111,g58)
    c: Parallel(g111,g58)
    c: Coincident(g30,g58)
    c: Coincident(g112,g60)
    c: Coincident(g112,g22)
    c: Parallel(g112,g60)
    c: Coincident(g28,g60)
    c: Coincident(g113,g102)
    c: Coincident(g113,g1)
    c: Coincident(g114,g26)
    c: Coincident(g114,g1)
    c: Coincident(g115,g2)
    c: Coincident(g115,g26)
    c: Coincident(g116,g101)
    c: Coincident(g116,g0)
    c: Perpendicular(g0,g116)
    c: Coincident(g117,g103)
    c: Coincident(g117,g1)
    c: Perpendicular(g117,g103)
    c: Equal(g1,g0)
    c: Equal(g47,g116)
FEATURE [Sketcher::SketchObject] Sketch002
  ExternalGeometry = -> [Sketch,Sketch001]
  FullyConstrained = false
  MapMode = 5
  Support = -> [XY_Plane]
  sketch-geometry (108):
    g0: ArcOfCircle CenterX=0 CenterY=0 CenterZ=0 NormalX=0 NormalY=0 NormalZ=1 AngleXU=0 Radius=117.223 StartAngle=0 EndAngle=1.5708
    g1: Circle CenterX=14.2857 CenterY=10 CenterZ=0 NormalX=0 NormalY=0 NormalZ=1 AngleXU=0 Radius=1
    g2: Circle CenterX=14.2857 CenterY=52.2154 CenterZ=0 NormalX=0 NormalY=0 NormalZ=1 AngleXU=0 Radius=1
    g3: Circle CenterX=30.9343 CenterY=113.067 CenterZ=0 NormalX=0 NormalY=0 NormalZ=1 AngleXU=0 Radius=1
    g4: BSplineCurve PolesCount=3 KnotsCount=2 Degree=2 IsPeriodic=0
    g5: GeomPoint X=14.2857 Y=10 Z=0
    g6: GeomPoint X=30.9343 Y=113.067 Z=0
    g7: Circle CenterX=28.9234 CenterY=9.9938 CenterZ=0 NormalX=0 NormalY=0 NormalZ=1 AngleXU=0 Radius=1
    g8: Circle CenterX=30.5838 CenterY=57.1382 CenterZ=0 NormalX=0 NormalY=0 NormalZ=1 AngleXU=0 Radius=1
    g9: Circle CenterX=55.3186 CenterY=103.349 CenterZ=0 NormalX=0 NormalY=0 NormalZ=1 AngleXU=0 Radius=1
    g10: BSplineCurve PolesCount=3 KnotsCount=2 Degree=2 IsPeriodic=0
    g11: GeomPoint X=28.9234 Y=9.9938 Z=0
    g12: GeomPoint X=55.3186 Y=103.349 Z=0
    g13: Circle CenterX=44.1654 CenterY=9.91405 CenterZ=0 NormalX=0 NormalY=0 NormalZ=1 AngleXU=0 Radius=1
    g14: Circle CenterX=50.5223 CenterY=58.0876 CenterZ=0 NormalX=0 NormalY=0 NormalZ=1 AngleXU=0 Radius=1
    g15: Circle CenterX=76.929 CenterY=88.4484 CenterZ=0 NormalX=0 NormalY=0 NormalZ=1 AngleXU=0 Radius=1
    g16: BSplineCurve PolesCount=3 KnotsCount=2 Degree=2 IsPeriodic=0
    g17: GeomPoint X=44.1654 Y=9.91405 Z=0
    g18: GeomPoint X=76.929 Y=88.4484 Z=0
    g19: Circle CenterX=59.4009 CenterY=9.74172 CenterZ=0 NormalX=0 NormalY=0 NormalZ=1 AngleXU=0 Radius=1
    g20: Circle CenterX=68.9065 CenterY=50.7499 CenterZ=0 NormalX=0 NormalY=0 NormalZ=1 AngleXU=0 Radius=1
    g21: Circle CenterX=94.3861 CenterY=69.5158 CenterZ=0 NormalX=0 NormalY=0 NormalZ=1 AngleXU=0 Radius=1
    g22: BSplineCurve PolesCount=3 KnotsCount=2 Degree=2 IsPeriodic=0
    g23: GeomPoint X=59.4009 Y=9.74172 Z=0
    g24: GeomPoint X=94.3861 Y=69.5158 Z=0
    g25: Circle CenterX=74.6473 CenterY=9.46782 CenterZ=0 NormalX=0 NormalY=0 NormalZ=1 AngleXU=0 Radius=1
    g26: Circle CenterX=83.9993 CenterY=36.9765 CenterZ=0 NormalX=0 NormalY=0 NormalZ=1 AngleXU=0 Radius=1
    g27: Circle CenterX=107.288 CenterY=47.2281 CenterZ=0 NormalX=0 NormalY=0 NormalZ=1 AngleXU=0 Radius=1
    g28: BSplineCurve PolesCount=3 KnotsCount=2 Degree=2 IsPeriodic=0
    g29: GeomPoint X=74.6473 Y=9.46782 Z=0
    g30: GeomPoint X=107.288 Y=47.2281 Z=0
    g31: Circle CenterX=89.9671 CenterY=9.05059 CenterZ=0 NormalX=0 NormalY=0 NormalZ=1 AngleXU=0 Radius=1
    g32: Circle CenterX=95.1125 CenterY=20.0006 CenterZ=0 NormalX=0 NormalY=0 NormalZ=1 AngleXU=0 Radius=1
    g33: Circle CenterX=114.714 CenterY=24.1224 CenterZ=0 NormalX=0 NormalY=0 NormalZ=1 AngleXU=0 Radius=1
    g34: BSplineCurve PolesCount=3 KnotsCount=2 Degree=2 IsPeriodic=0
    g35: GeomPoint X=89.9671 Y=9.05059 Z=0
    g36: GeomPoint X=114.714 Y=24.1224 Z=0
    g37: LineSegment StartX=14.2857 StartY=52.2154 StartZ=0 EndX=30.9343 EndY=113.067 EndZ=0
    g38: LineSegment StartX=30.5838 StartY=57.1382 StartZ=0 EndX=55.3186 EndY=103.349 EndZ=0
    g39: LineSegment StartX=50.5223 StartY=58.0876 StartZ=0 EndX=76.929 EndY=88.4484 EndZ=0
    g40: LineSegment StartX=68.9065 StartY=50.7499 StartZ=0 EndX=94.3861 EndY=69.5158 EndZ=0
    g41: LineSegment StartX=83.9993 StartY=36.9765 StartZ=0 EndX=107.288 EndY=47.2281 EndZ=0
    g42: LineSegment StartX=95.1125 StartY=20.0006 StartZ=0 EndX=114.714 EndY=24.1224 EndZ=0
    g43: LineSegment StartX=26.0845 StartY=114.284 StartZ=0 EndX=31.8413 EndY=112.815 EndZ=0
    g44: ArcOfCircle CenterX=106.739 CenterY=0.371508 CenterZ=0 NormalX=0 NormalY=0 NormalZ=1 AngleXU=0 Radius=4.31105 StartAngle=0.440313 EndAngle=2.32253
    g45: ArcOfCircle CenterX=114.906 CenterY=4.21964 CenterZ=0 NormalX=0 NormalY=0 NormalZ=1 AngleXU=0 Radius=4.71741 StartAngle=3.58191 EndAngle=4.58179
    g46: LineSegment StartX=30.9343 StartY=113.067 StartZ=0 EndX=31.6672 EndY=115.746 EndZ=0
    g47: LineSegment StartX=55.3186 StartY=103.349 StartZ=0 EndX=56.6292 EndY=105.798 EndZ=0
    g48: LineSegment StartX=76.929 StartY=88.4484 StartZ=0 EndX=78.7516 EndY=90.5439 EndZ=0
    g49: LineSegment StartX=94.3861 StartY=69.5158 StartZ=0 EndX=96.6223 EndY=71.1627 EndZ=0
    g50: LineSegment StartX=107.288 StartY=47.2281 StartZ=0 EndX=109.83 EndY=48.347 EndZ=0
    g51: LineSegment StartX=114.714 StartY=24.1224 StartZ=0 EndX=117.432 EndY=24.6939 EndZ=0
    g52: ArcOfCircle CenterX=0 CenterY=0 CenterZ=0 NormalX=0 NormalY=0 NormalZ=1 AngleXU=0 Radius=120 StartAngle=6.27937 EndAngle=6.43677
    g53: Circle CenterX=82.5619 CenterY=2.69685 CenterZ=0 NormalX=0 NormalY=0 NormalZ=1 AngleXU=0 Radius=1
    g54: Circle CenterX=99.0099 CenterY=40.1968 CenterZ=0 NormalX=0 NormalY=0 NormalZ=1 AngleXU=0 Radius=1
    g55: Circle CenterX=110.886 CenterY=45.8718 CenterZ=0 NormalX=0 NormalY=0 NormalZ=1 AngleXU=0 Radius=1
    g56: BSplineCurve PolesCount=3 KnotsCount=2 Degree=2 IsPeriodic=0
    g57: GeomPoint X=82.5619 Y=2.69685 Z=0
    g58: GeomPoint X=110.886 Y=45.8718 Z=0
    g59: Circle CenterX=68.1159 CenterY=2.68309 CenterZ=0 NormalX=0 NormalY=0 NormalZ=1 AngleXU=0 Radius=1
    g60: Circle CenterX=87.8149 CenterY=65.5945 CenterZ=0 NormalX=0 NormalY=0 NormalZ=1 AngleXU=0 Radius=1
    g61: Circle CenterX=98.1518 CenterY=69.0379 CenterZ=0 NormalX=0 NormalY=0 NormalZ=1 AngleXU=0 Radius=1
    g62: BSplineCurve PolesCount=3 KnotsCount=2 Degree=2 IsPeriodic=0
    g63: GeomPoint X=68.1159 Y=2.68309 Z=0
    g64: GeomPoint X=98.1518 Y=69.0379 Z=0
    g65: Circle CenterX=53.6545 CenterY=2.6649 CenterZ=0 NormalX=0 NormalY=0 NormalZ=1 AngleXU=0 Radius=1
    g66: Circle CenterX=66.2602 CenterY=81.9693 CenterZ=0 NormalX=0 NormalY=0 NormalZ=1 AngleXU=0 Radius=1
    g67: Circle CenterX=81.7786 CenterY=87.8195 CenterZ=0 NormalX=0 NormalY=0 NormalZ=1 AngleXU=0 Radius=1
    g68: BSplineCurve PolesCount=3 KnotsCount=2 Degree=2 IsPeriodic=0
    g69: GeomPoint X=53.6545 Y=2.6649 Z=0
    g70: GeomPoint X=81.7786 Y=87.8195 Z=0
    g71: Circle CenterX=39.1713 CenterY=2.64361 CenterZ=0 NormalX=0 NormalY=0 NormalZ=1 AngleXU=0 Radius=1
    g72: Circle CenterX=48.5487 CenterY=97.5087 CenterZ=0 NormalX=0 NormalY=0 NormalZ=1 AngleXU=0 Radius=1
    g73: Circle CenterX=58.7112 CenterY=104.657 CenterZ=0 NormalX=0 NormalY=0 NormalZ=1 AngleXU=0 Radius=1
    g74: BSplineCurve PolesCount=3 KnotsCount=2 Degree=2 IsPeriodic=0
    g75: GeomPoint X=39.1713 Y=2.64361 Z=0
    g76: GeomPoint X=58.7112 Y=104.657 Z=0
    g77: Circle CenterX=24.6652 CenterY=2.73433 CenterZ=0 NormalX=0 NormalY=0 NormalZ=1 AngleXU=0 Radius=1
    g78: Circle CenterX=28.8321 CenterY=109.038 CenterZ=0 NormalX=0 NormalY=0 NormalZ=1 AngleXU=0 Radius=1
    g79: Circle CenterX=32.7716 CenterY=115.438 CenterZ=0 NormalX=0 NormalY=0 NormalZ=1 AngleXU=0 Radius=1
    g80: BSplineCurve PolesCount=3 KnotsCount=2 Degree=2 IsPeriodic=0
    g81: GeomPoint X=24.6652 Y=2.73433 Z=0
    g82: GeomPoint X=32.7716 Y=115.438 Z=0
    g83: LineSegment StartX=74.6473 StartY=9.46782 StartZ=0 EndX=82.5619 EndY=2.69685 EndZ=0
    g84: LineSegment StartX=59.4009 StartY=9.74172 StartZ=0 EndX=68.1159 EndY=2.68309 EndZ=0
    g85: LineSegment StartX=44.1654 StartY=9.91405 StartZ=0 EndX=53.6545 EndY=2.6649 EndZ=0
    g86: LineSegment StartX=28.9234 StartY=9.9938 StartZ=0 EndX=39.1713 EndY=2.64361 EndZ=0
    g87: LineSegment StartX=14.2857 StartY=10 StartZ=0 EndX=24.6652 EndY=2.73433 EndZ=0
    g88: ArcOfCircle CenterX=0 CenterY=0 CenterZ=0 NormalX=0 NormalY=0 NormalZ=1 AngleXU=0 Radius=120 StartAngle=0.414674 EndAngle=0.61299
    g89: ArcOfCircle CenterX=0 CenterY=0 CenterZ=0 NormalX=0 NormalY=0 NormalZ=1 AngleXU=0 Radius=120 StartAngle=0.634808 EndAngle=0.821002
    g90: ArcOfCircle CenterX=0 CenterY=0 CenterZ=0 NormalX=0 NormalY=0 NormalZ=1 AngleXU=0 Radius=120 StartAngle=0.854941 EndAngle=1.05956
    g91: ArcOfCircle CenterX=0 CenterY=0 CenterZ=0 NormalX=0 NormalY=0 NormalZ=1 AngleXU=0 Radius=120 StartAngle=1.07934 EndAngle=1.29419
    g92: ArcOfCircle CenterX=0 CenterY=0 CenterZ=0 NormalX=0 NormalY=0 NormalZ=1 AngleXU=0 Radius=120 StartAngle=1.30374 EndAngle=1.5708
    g93: LineSegment StartX=0 StartY=120 StartZ=0 EndX=0 EndY=-0.5 EndZ=0
    g94: LineSegment StartX=13.7857 StartY=-22.2697 StartZ=0 EndX=100.5 EndY=-22.2697 EndZ=0
    g95: Circle CenterX=99.8012 CenterY=5.05341 CenterZ=0 NormalX=0 NormalY=0 NormalZ=1 AngleXU=0 Radius=1
    g96: Circle CenterX=111.516 CenterY=17.2173 CenterZ=0 NormalX=0 NormalY=0 NormalZ=1 AngleXU=0 Radius=1
    g97: Circle CenterX=118.588 CenterY=18.3576 CenterZ=0 NormalX=0 NormalY=0 NormalZ=1 AngleXU=0 Radius=1
    g98: BSplineCurve PolesCount=3 KnotsCount=2 Degree=2 IsPeriodic=0
    g99: GeomPoint X=99.8012 Y=5.05341 Z=0
    g100: GeomPoint X=118.588 Y=18.3576 Z=0
    g101: ArcOfCircle CenterX=0 CenterY=0 CenterZ=0 NormalX=0 NormalY=0 NormalZ=1 AngleXU=0 Radius=120 StartAngle=0.207263 EndAngle=0.392246
    g102: LineSegment StartX=114.292 StartY=-0.457591 StartZ=0 EndX=119.999 EndY=-0.457591 EndZ=0
    g103: LineSegment StartX=100.5 StartY=0.22577 StartZ=0 EndX=100.5 EndY=-22.2697 EndZ=0
    g104: LineSegment StartX=13.7857 StartY=-0.5 StartZ=0 EndX=0 EndY=-0.5 EndZ=0
    g105: LineSegment StartX=13.7857 StartY=-0.5 StartZ=0 EndX=13.7857 EndY=-22.2697 EndZ=0
    g106: LineSegment StartX=99.8012 StartY=5.05341 StartZ=0 EndX=89.9671 EndY=9.05059 EndZ=0
    g107: LineSegment StartX=103.795 StartY=3.52077 StartZ=0 EndX=100.5 EndY=0.22577 EndZ=0
  constraints (224):
    c: Coincident(g0,g-1)
    c: PointOnObject(g0,g-2)
    c: PointOnObject(g0,g-1)
    c: PointOnObject(g-3,g0)
    c: Weight(g1) = 1
    c: Coincident(g4,g-4)
    c: Equal(g1,g2)
    c: Equal(g1,g3)
    c: PointOnObject(g4,g0)
    c: InternalAlignment(g1,g4)
    c: InternalAlignment(g2,g4)
    c: InternalAlignment(g3,g4)
    c: InternalAlignment(g5,g4)
    c: InternalAlignment(g6,g4)
    c: PointOnObject(g2,g-12)
    c: Weight(g7) = 1
    c: Coincident(g10,g-13)
    c: Equal(g7,g8)
    c: PointOnObject(g8,g-13)
    c: Equal(g7,g9)
    c: PointOnObject(g10,g0)
    c: InternalAlignment(g7,g10)
    c: InternalAlignment(g8,g10)
    c: InternalAlignment(g9,g10)
    c: InternalAlignment(g11,g10)
    c: InternalAlignment(g12,g10)
    c: Weight(g13) = 1
    c: Coincident(g16,g-14)
    c: Equal(g13,g14)
    c: PointOnObject(g14,g-14)
    c: Equal(g13,g15)
    c: PointOnObject(g16,g0)
    c: InternalAlignment(g13,g16)
    c: InternalAlignment(g14,g16)
    c: InternalAlignment(g15,g16)
    c: InternalAlignment(g17,g16)
    c: InternalAlignment(g18,g16)
    c: Weight(g19) = 1
    c: Coincident(g22,g-15)
    c: Equal(g19,g20)
    c: PointOnObject(g20,g-15)
    c: Equal(g19,g21)
    c: PointOnObject(g22,g0)
    c: InternalAlignment(g19,g22)
    c: InternalAlignment(g20,g22)
    c: InternalAlignment(g21,g22)
    c: InternalAlignment(g23,g22)
    c: InternalAlignment(g24,g22)
    c: Weight(g25) = 1
    c: Coincident(g28,g-16)
    c: Equal(g25,g26)
    c: PointOnObject(g26,g-16)
    c: Equal(g25,g27)
    c: PointOnObject(g28,g0)
    c: InternalAlignment(g25,g28)
    c: InternalAlignment(g26,g28)
    c: InternalAlignment(g27,g28)
    c: InternalAlignment(g29,g28)
    c: InternalAlignment(g30,g28)
    c: Weight(g31) = 1
    c: Coincident(g34,g-17)
    c: Equal(g31,g32)
    c: PointOnObject(g32,g-17)
    c: Equal(g31,g33)
    c: PointOnObject(g34,g0)
    c: InternalAlignment(g31,g34)
    c: InternalAlignment(g32,g34)
    c: InternalAlignment(g33,g34)
    c: InternalAlignment(g35,g34)
    c: InternalAlignment(g36,g34)
    c: Coincident(g37,g2)
    c: Coincident(g37,g4)
    c: Coincident(g38,g8)
    c: Coincident(g38,g10)
    c: Coincident(g39,g14)
    c: Coincident(g39,g16)
    c: Coincident(g40,g20)
    c: Coincident(g40,g22)
    c: Coincident(g41,g26)
    c: Coincident(g41,g28)
    c: Coincident(g42,g32)
    c: Coincident(g42,g34)
    c: Perpendicular(g0,g37)
    c: Perpendicular(g0,g38)
    c: Perpendicular(g0,g39)
    c: Perpendicular(g0,g40)
    c: Perpendicular(g0,g41)
    c: Perpendicular(g0,g42)
    c: Coincident(g43,g-3)
    c: Distance(g43,g4) = 5
    c: Distance(g-22,g34) = 2
    c: Distance(g-18,g10) = 5
    c: Distance(g-19,g16) = 5
    c: Distance(g-20,g22) = 4.5
    c: Distance(g-21,g28) = 4
    c: Tangent(g45,g44) = 1.5708
    c: Coincident(g46,g4)
    c: Coincident(g47,g10)
    c: Coincident(g48,g16)
    c: Coincident(g49,g22)
    c: Coincident(g50,g28)
    c: Coincident(g51,g34)
    c: Perpendicular(g0,g51)
    c: Perpendicular(g0,g50)
    c: Perpendicular(g0,g49)
    c: Perpendicular(g0,g48)
    c: Perpendicular(g0,g47)
    c: Perpendicular(g0,g46)
    c: Equal(g46,g47)
    c: Equal(g47,g48)
    c: Equal(g48,g49)
    c: Equal(g49,g50)
    c: Equal(g50,g51)
    c: Coincident(g52,g0)
    c: PointOnObject(g92,g-2)
    c: PointOnObject(g46,g52)
    c: Radius(g52) = 120
    c: Weight(g53) = 1
    c: Coincident(g56,g-23)
    c: Equal(g53,g54)
    c: Equal(g53,g55)
    c: InternalAlignment(g53,g56)
    c: InternalAlignment(g54,g56)
    c: InternalAlignment(g55,g56)
    c: InternalAlignment(g57,g56)
    c: InternalAlignment(g58,g56)
    c: Weight(g59) = 1
    c: Coincident(g62,g-24)
    c: Equal(g59,g60)
    c: Equal(g59,g61)
    c: PointOnObject(g62,g52)
    c: InternalAlignment(g59,g62)
    c: InternalAlignment(g60,g62)
    c: InternalAlignment(g61,g62)
    c: InternalAlignment(g63,g62)
    c: InternalAlignment(g64,g62)
    c: Weight(g65) = 1
    c: Coincident(g68,g-25)
    c: Equal(g65,g66)
    c: Equal(g65,g67)
    c: PointOnObject(g68,g52)
    c: InternalAlignment(g65,g68)
    c: InternalAlignment(g66,g68)
    c: InternalAlignment(g67,g68)
    c: InternalAlignment(g69,g68)
    c: InternalAlignment(g70,g68)
    c: Weight(g71) = 1
    c: Coincident(g74,g-26)
    c: Equal(g71,g72)
    c: Equal(g71,g73)
    c: PointOnObject(g74,g52)
    c: InternalAlignment(g71,g74)
    c: InternalAlignment(g72,g74)
    c: InternalAlignment(g73,g74)
    c: InternalAlignment(g75,g74)
    c: InternalAlignment(g76,g74)
    c: Weight(g77) = 1
    c: Coincident(g80,g-27)
    c: Equal(g77,g78)
    c: Equal(g77,g79)
    c: PointOnObject(g80,g52)
    c: InternalAlignment(g77,g80)
    c: InternalAlignment(g78,g80)
    c: InternalAlignment(g79,g80)
    c: InternalAlignment(g81,g80)
    c: InternalAlignment(g82,g80)
    c: Coincident(g83,g28)
    c: Coincident(g83,g56)
    c: Coincident(g84,g22)
    c: Coincident(g84,g62)
    c: Coincident(g85,g16)
    c: Coincident(g85,g68)
    c: Coincident(g86,g10)
    c: Coincident(g86,g74)
    c: Coincident(g87,g4)
    c: Coincident(g87,g80)
    c: Equal(g52,g88)
    c: PointOnObject(g88,g50)
    c: Coincident(g52,g88)
    c: Coincident(g101,g56)
    c: Equal(g88,g89)
    c: PointOnObject(g89,g49)
    c: Coincident(g88,g89)
    c: Equal(g89,g90)
    c: PointOnObject(g90,g48)
    c: Coincident(g89,g90)
    c: Equal(g90,g91)
    c: PointOnObject(g91,g47)
    c: Coincident(g90,g91)
    c: Equal(g91,g92)
    c: Coincident(g91,g92)
    c: PointOnObject(g92,g46)
    c: Coincident(g93,g92)
    c: Horizontal(g94)
    c: Weight(g95) = 1
    c: Equal(g95,g96)
    c: Equal(g95,g97)
    c: InternalAlignment(g95,g98)
    c: InternalAlignment(g96,g98)
    c: InternalAlignment(g97,g98)
    c: InternalAlignment(g99,g98)
    c: InternalAlignment(g100,g98)
    c: Equal(g52,g101)
    c: PointOnObject(g101,g51)
    c: Coincident(g52,g101)
    c: Coincident(g52,g98)
    c: Coincident(g102,g45)
    c: Horizontal(g102)
    c: Coincident(g102,g52)
    c: Vertical(g103)
    c: Coincident(g94,g103)
    c: Coincident(g104,g-29)
    c: Horizontal(g104)
    c: Coincident(g105,g104)
    c: Vertical(g105)
    c: Coincident(g93,g104)
    c: Coincident(g94,g105)
    c: Vertical(g93)
    c: Coincident(g98,g106)
    c: Coincident(g34,g106)
    c: PointOnObject(g-28,g103)
    c: Coincident(g107,g44)
    c: Coincident(g107,g103)
    c: Parallel(g-10,g107)
FEATURE [Sketcher::SketchObject] Sketch003
  ExternalGeometry = -> [Sketch001,Sketch]
  FullyConstrained = true
  MapMode = 5
  Support = -> [XY_Plane]
  sketch-geometry (28):
    g0: LineSegment StartX=10.2857 StartY=0 StartZ=0 EndX=14.2857 EndY=2.955e-12 EndZ=0
    g1: LineSegment StartX=14.2857 StartY=2.955e-12 StartZ=0 EndX=14.2857 EndY=115.18 EndZ=0
    g2: LineSegment StartX=14.2857 StartY=115.18 StartZ=0 EndX=10.2857 EndY=115.18 EndZ=0
    g3: LineSegment StartX=10.2857 StartY=115.18 StartZ=0 EndX=10.2857 EndY=0 EndZ=0
    g4: LineSegment StartX=24.6652 StartY=2.73433 StartZ=0 EndX=28.6628 EndY=2.59354 EndZ=0
    g5: LineSegment StartX=28.6628 StartY=2.59354 StartZ=0 EndX=32.403 EndY=108.793 EndZ=0
    g6: LineSegment StartX=32.403 StartY=108.793 StartZ=0 EndX=28.4054 EndY=108.933 EndZ=0
    g7: LineSegment StartX=28.4054 StartY=108.933 StartZ=0 EndX=24.6652 EndY=2.73433 EndZ=0
    g8: LineSegment StartX=39.1713 StartY=2.64361 StartZ=0 EndX=43.1369 EndY=2.12031 EndZ=0
    g9: LineSegment StartX=43.1369 StartY=2.12031 StartZ=0 EndX=55.6558 EndY=96.9892 EndZ=0
    g10: LineSegment StartX=55.6558 StartY=96.9892 StartZ=0 EndX=51.6902 EndY=97.5125 EndZ=0
    g11: LineSegment StartX=51.6902 StartY=97.5125 StartZ=0 EndX=39.1713 EndY=2.64361 EndZ=0
    g12: LineSegment StartX=53.6545 StartY=2.6649 StartZ=0 EndX=57.5512 EndY=1.76166 EndZ=0
    g13: LineSegment StartX=57.5512 StartY=1.76166 StartZ=0 EndX=75.7744 EndY=80.3789 EndZ=0
    g14: LineSegment StartX=75.7744 StartY=80.3789 StartZ=0 EndX=71.8777 EndY=81.2821 EndZ=0
    g15: LineSegment StartX=71.8777 StartY=81.2821 StartZ=0 EndX=53.6545 EndY=2.6649 EndZ=0
    g16: LineSegment StartX=68.1159 StartY=2.68309 StartZ=0 EndX=71.903 EndY=1.39559 EndZ=0
    g17: LineSegment StartX=71.903 StartY=1.39559 StartZ=0 EndX=91.8032 EndY=59.9313 EndZ=0
    g18: LineSegment StartX=91.8032 StartY=59.9313 StartZ=0 EndX=88.0161 EndY=61.2188 EndZ=0
    g19: LineSegment StartX=88.0161 StartY=61.2188 StartZ=0 EndX=68.1159 EndY=2.68309 EndZ=0
    g20: LineSegment StartX=82.5619 StartY=2.69685 StartZ=0 EndX=86.1822 EndY=0.99571 EndZ=0
    g21: LineSegment StartX=86.1822 StartY=0.99571 StartZ=0 EndX=103.13 EndY=37.0622 EndZ=0
    g22: LineSegment StartX=103.13 StartY=37.0622 StartZ=0 EndX=99.5095 EndY=38.7633 EndZ=0
    g23: LineSegment StartX=99.5095 StartY=38.7633 StartZ=0 EndX=82.5619 EndY=2.69685 EndZ=0
    g24: LineSegment StartX=100 StartY=2.9541e-12 StartZ=0 EndX=102.828 EndY=-2.82843 EndZ=0
    g25: LineSegment StartX=102.828 StartY=-2.82843 StartZ=0 EndX=115.563 EndY=9.90657 EndZ=0
    g26: LineSegment StartX=115.563 StartY=9.90657 StartZ=0 EndX=112.735 EndY=12.735 EndZ=0
    g27: LineSegment StartX=112.735 StartY=12.735 StartZ=0 EndX=100 EndY=2.9541e-12 EndZ=0
  constraints (56):
    c: Coincident(g-16,g0)
    c: Coincident(g0,g-17)
    c: Coincident(g0,g1)
    c: Coincident(g1,g-15)
    c: Coincident(g1,g2)
    c: Coincident(g2,g-15)
    c: Coincident(g2,g3)
    c: Coincident(g3,g0)
    c: Coincident(g-3,g4)
    c: Coincident(g4,g-3)
    c: Coincident(g4,g5)
    c: Coincident(g5,g-14)
    c: Coincident(g5,g6)
    c: Coincident(g6,g-14)
    c: Coincident(g6,g7)
    c: Coincident(g7,g4)
    c: Coincident(g-4,g8)
    c: Coincident(g8,g-4)
    c: Coincident(g8,g9)
    c: Coincident(g9,g-13)
    c: Coincident(g9,g10)
    c: Coincident(g10,g-13)
    c: Coincident(g10,g11)
    c: Coincident(g11,g8)
    c: Coincident(g-5,g12)
    c: Coincident(g12,g-5)
    c: Coincident(g12,g13)
    c: Coincident(g13,g-12)
    c: Coincident(g13,g14)
    c: Coincident(g14,g-12)
    c: Coincident(g14,g15)
    c: Coincident(g15,g12)
    c: Coincident(g-6,g16)
    c: Coincident(g16,g-6)
    c: Coincident(g16,g17)
    c: Coincident(g17,g-11)
    c: Coincident(g17,g18)
    c: Coincident(g18,g-11)
    c: Coincident(g18,g19)
    c: Coincident(g19,g16)
    c: Coincident(g-7,g20)
    c: Coincident(g20,g-7)
    c: Coincident(g20,g21)
    c: Coincident(g21,g-10)
    c: Coincident(g21,g22)
    c: Coincident(g22,g-10)
    c: Coincident(g22,g23)
    c: Coincident(g23,g20)
    c: Coincident(g-8,g24)
    c: Coincident(g24,g-8)
    c: Coincident(g24,g25)
    c: Coincident(g25,g-9)
    c: Coincident(g25,g26)
    c: Coincident(g26,g-9)
    c: Coincident(g26,g27)
    c: Coincident(g27,g24)
FEATURE [Sketcher::SketchObject] Sketch004
  ExternalGeometry = -> [Sketch001]
  FullyConstrained = true
  MapMode = 5
  Support = -> [XY_Plane]
  sketch-geometry (4):
    g0: LineSegment StartX=-15.2143 StartY=135.68 StartZ=0 EndX=139.806 EndY=135.68 EndZ=0
    g1: LineSegment StartX=139.806 StartY=135.68 StartZ=0 EndX=139.806 EndY=-85 EndZ=0
    g2: LineSegment StartX=139.806 StartY=-85 StartZ=0 EndX=-15.2143 EndY=-85 EndZ=0
    g3: LineSegment StartX=-15.2143 StartY=-85 StartZ=0 EndX=-15.2143 EndY=135.68 EndZ=0
  constraints (12):
    c: Coincident(g0,g1)
    c: Coincident(g1,g2)
    c: Coincident(g2,g3)
    c: Coincident(g3,g0)
    c: Horizontal(g0)
    c: Horizontal(g2)
    c: Vertical(g1)
    c: Vertical(g3)
    c: DistanceX(g-4,g1) = 20
    c: DistanceY(g1,g-5) = 70
    c: DistanceX(g0,g-3) = 20
    c: DistanceY(g-3,g0) = 20
FEATURE [Sketcher::SketchObject] Sketch005
  ExternalGeometry = -> [Sketch004]
  FullyConstrained = true
  MapMode = 5
  Support = -> [XY_Plane]
  sketch-geometry (8):
    g0: LineSegment StartX=139.806 StartY=-85 StartZ=0 EndX=4.78571 EndY=-85 EndZ=0
    g1: LineSegment StartX=4.78571 StartY=-85 StartZ=0 EndX=4.78571 EndY=115.68 EndZ=0
    g2: LineSegment StartX=4.78571 StartY=115.68 StartZ=0 EndX=139.806 EndY=115.68 EndZ=0
    g3: LineSegment StartX=139.806 StartY=115.68 StartZ=0 EndX=139.806 EndY=-85 EndZ=0
    g4: LineSegment StartX=119.806 StartY=115.68 StartZ=0 EndX=119.806 EndY=135.68 EndZ=0
    g5: LineSegment StartX=119.806 StartY=135.68 StartZ=0 EndX=-15.2143 EndY=135.68 EndZ=0
    g6: LineSegment StartX=-15.2143 StartY=135.68 StartZ=0 EndX=-15.2143 EndY=0.659653 EndZ=0
    g7: LineSegment StartX=-15.2143 StartY=0.659653 StartZ=0 EndX=4.78571 EndY=0.659653 EndZ=0
  constraints (23):
    c: Coincident(g0,g1)
    c: Coincident(g1,g2)
    c: Coincident(g2,g3)
    c: Coincident(g3,g0)
    c: Horizontal(g0)
    c: Horizontal(g2)
    c: Vertical(g1)
    c: Vertical(g3)
    c: Coincident(g0,g-4)
    c: DistanceY(g2,g-4) = 20
    c: DistanceX(g-3,g0) = 20
    c: PointOnObject(g4,g2)
    c: PointOnObject(g4,g-5)
    c: Vertical(g4)
    c: Coincident(g4,g5)
    c: Coincident(g5,g-5)
    c: Coincident(g5,g6)
    c: Vertical(g6)
    c: Coincident(g6,g7)
    c: PointOnObject(g7,g1)
    c: Horizontal(g7)
    c: Equal(g2,g5)
    c: Equal(g5,g6)
FEATURE [PartDesign::Body] Body
  Group = -> [Sketch,Sketch001,Sketch002,Sketch003,Sketch004,Sketch005]
  Origin = -> Origin
